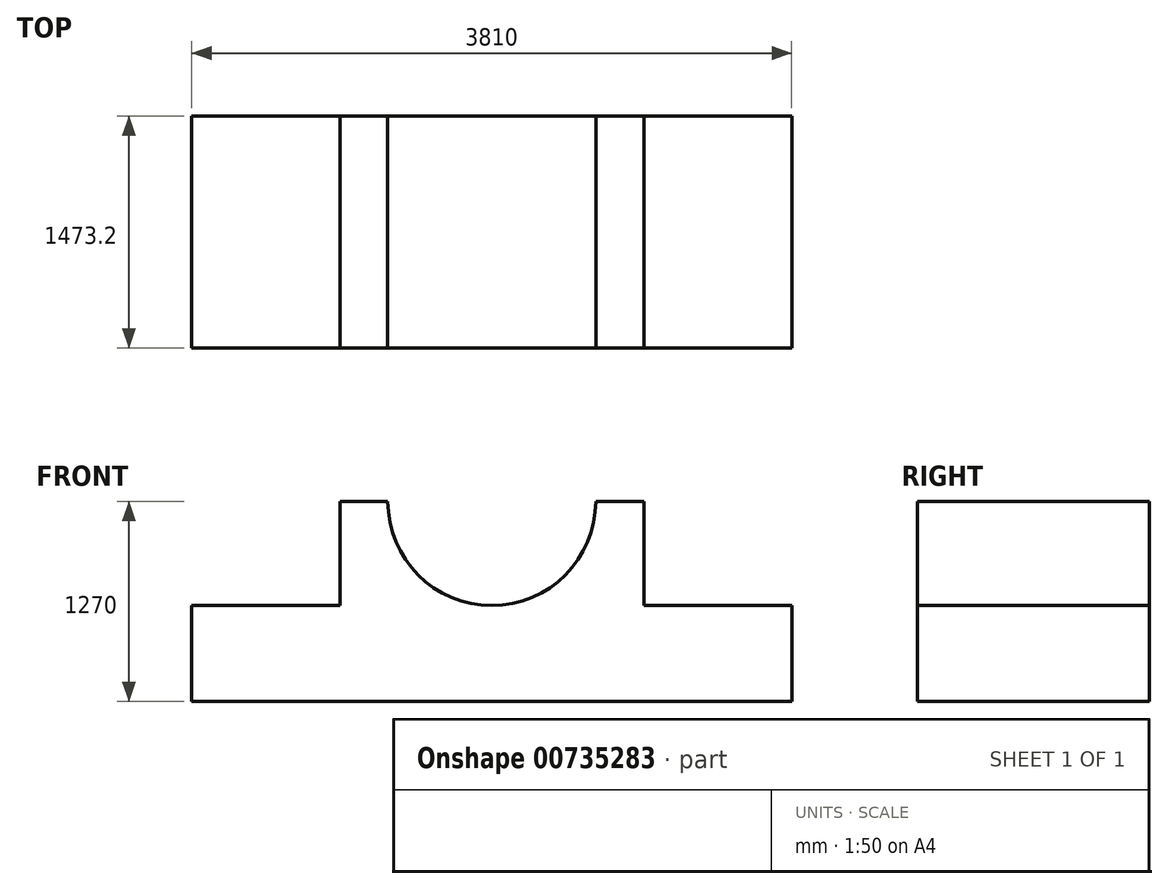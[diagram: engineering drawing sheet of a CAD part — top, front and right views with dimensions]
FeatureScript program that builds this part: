
annotation { "Feature Type Name" : "Feature", "Feature Type Description" : "" }
export const myFeature = defineFeature(function(context is Context, id is Id, definition is map)
    precondition{}
    {
        {
            var Q0;
            Q0=qCreatedBy(makeId("Front.planeOp"),FACE);
            var sketch = newSketch(context, id + "F0", { "sketchPlane" : qUnion([Q0])});
            skLineSegment(sketch, "E0", {"start": v(-71.99, -32.91) * mm, "end": v(3738.01, -32.91) * mm});
            skLineSegment(sketch, "E1", {"start": v(3738.01, -32.91) * mm, "end": v(3738.01, 576.69) * mm});
            skLineSegment(sketch, "E2", {"start": v(-71.99, -32.91) * mm, "end": v(-71.99, 576.69) * mm});
            skLineSegment(sketch, "E3", {"start": v(-71.99, 576.69) * mm, "end": v(867.81, 576.69) * mm});
            skLineSegment(sketch, "E4", {"start": v(3738.01, 576.69) * mm, "end": v(2798.21, 576.69) * mm});
            skLineSegment(sketch, "E5", {"start": v(867.81, 576.69) * mm, "end": v(867.81, 1237.09) * mm});
            skLineSegment(sketch, "E6", {"start": v(2798.21, 576.69) * mm, "end": v(2798.21, 1237.09) * mm});
            skLineSegment(sketch, "E7", {"start": v(867.81, 1237.09) * mm, "end": v(1172.61, 1237.09) * mm});
            skLineSegment(sketch, "E8", {"start": v(2798.21, 1237.09) * mm, "end": v(2493.41, 1237.09) * mm});
            skCircle(sketch, "E9", {"center": v(1833.01, 1237.09) * mm, "radius": 660.4 * mm});
            skSolve(sketch);
        }
        {
            var Q0;
            Q0=makeQuery(id+"F0.imprint","IMPRINT",FACE,{"disambiguationData":[TD([[makeQuery(id+"F0.imprint","IMPRINT",EDGE,{"derivedFrom":sQuery(id+"F0.wireOp",EDGE,"E0")}),1.0]])]});
            extrude(context, id + "F1", {"entities" : qUnion([Q0]), "depth" : 1473.2 * mm, "offsetDistance" : 25.4 * mm});
        }
    });
